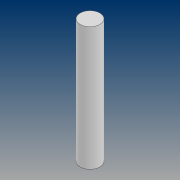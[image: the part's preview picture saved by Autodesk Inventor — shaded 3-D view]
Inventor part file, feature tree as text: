
AUTODESK INVENTOR PART (.ipt)
format: ipt  version: 2021 (Build 250183000, 183)  size: 72,192 bytes
history: native  units: mm
features: extrude x1, sketch x1
ambient origin geometry x8: Origin, YZ Plane, XZ Plane, XY Plane, X Axis, Y Axis, Z Axis, Center Point
bodies: Solid1 (feature_tree)
feature tree (2):
  extrude  "Extrusion1"  Depth=50.0mm TaperAngle=0.0deg
  sketch  "Sketch1"  dims[d0=8.0mm d1=50.0mm d2=0.0mm]
